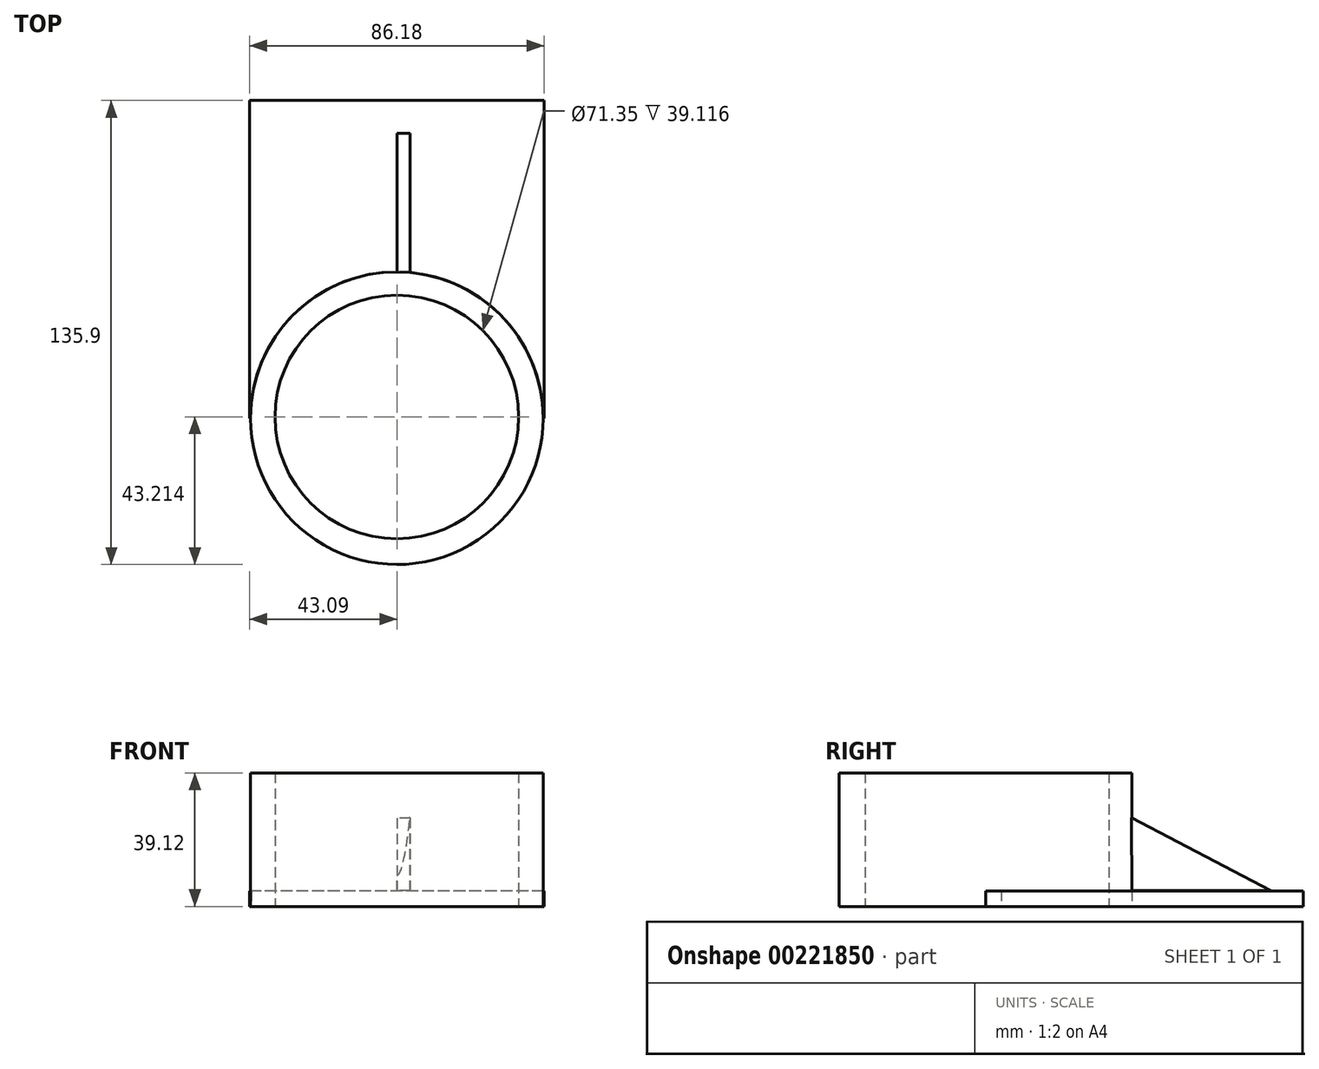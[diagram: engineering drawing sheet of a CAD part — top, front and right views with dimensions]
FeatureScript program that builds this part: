
annotation { "Feature Type Name" : "Feature", "Feature Type Description" : "" }
export const myFeature = defineFeature(function(context is Context, id is Id, definition is map)
    precondition{}
    {
        {
            var Q0;
            Q0=qCreatedBy(makeId("Top.planeOp"),FACE);
            var sketch = newSketch(context, id + "F0", { "sketchPlane" : qUnion([Q0])});
            skLineSegment(sketch, "E0.bottom", {"start": v(43.09, 46.52) * mm, "end": v(-43.09, 46.52) * mm});
            skLineSegment(sketch, "E0.top", {"start": v(43.09, -46.52) * mm, "end": v(42.83, -46.52) * mm});
            skLineSegment(sketch, "E0.left", {"start": v(43.09, 46.52) * mm, "end": v(43.09, -46.52) * mm});
            skLineSegment(sketch, "E0.right", {"start": v(-43.09, 46.52) * mm, "end": v(-43.09, -46.52) * mm});
            skPoint(sketch, "E0.middle", {"position": v(0, 0) * mm});
            skCircle(sketch, "E1", {"center": v(0, -46.52) * mm, "radius": 42.83 * mm});
            skLineSegment(sketch, "E2.trimOffspring", {"start": v(-42.83, -46.52) * mm, "end": v(-43.09, -46.52) * mm});
            skSolve(sketch);
        }
        {
            var Q0;
            Q0=makeQuery(id+"F0.imprint","IMPRINT",FACE,{"disambiguationData":[TD([[makeQuery(id+"F0.imprint","IMPRINT",EDGE,{"derivedFrom":sQuery(id+"F0.wireOp",EDGE,"E0.bottom")}),1.0]])]});
            extrude(context, id + "F1", {"entities" : qUnion([Q0]), "depth" : 4.57 * mm});
        }
        {
            var Q0;
            Q0=qCreatedBy(makeId("Top.planeOp"),FACE);
            var sketch = newSketch(context, id + "F2", { "sketchPlane" : qUnion([Q0])});
            skCircle(sketch, "E3", {"center": v(0, -46.54) * mm, "radius": 42.83 * mm});
            skSolve(sketch);
        }
        {
            var Q0;
            Q0=makeQuery(id+"F2.imprint","IMPRINT",FACE,{"disambiguationData":[TD([[makeQuery(id+"F2.imprint","IMPRINT",EDGE,{"derivedFrom":sQuery(id+"F2.wireOp",EDGE,"E3")}),1.0]])]});
            extrude(context, id + "F3", {"entities" : qUnion([Q0]), "operationType" : NewBodyOperationType.ADD, "depth" : 39.12 * mm});
        }
        {
            var Q0;
            Q0=qCreatedBy(makeId("Top.planeOp"),FACE);
            var sketch = newSketch(context, id + "F4", { "sketchPlane" : qUnion([Q0])});
            skCircle(sketch, "E4", {"center": v(0, -46.17) * mm, "radius": 35.68 * mm});
            skSolve(sketch);
        }
        {
            var Q0;
            Q0 = qSketchRegion(id + "F4", true);
            extrude(context, id + "F5", {"entities" : qUnion([Q0]), "operationType" : NewBodyOperationType.REMOVE, "depth" : 82.55 * mm});
        }
        {
            var Q0;
            Q0=qCreatedBy(makeId("Right.planeOp"),FACE);
            var sketch = newSketch(context, id + "F6", { "sketchPlane" : qUnion([Q0])});
            skLineSegment(sketch, "E5", {"start": v(-3.89, 25.93) * mm, "end": v(36.9, 4.6) * mm});
            skLineSegment(sketch, "E6", {"start": v(36.9, 4.6) * mm, "end": v(-3.66, 4.6) * mm});
            skLineSegment(sketch, "E7", {"start": v(-3.66, 4.6) * mm, "end": v(-3.89, 25.93) * mm});
            skSolve(sketch);
        }
        {
            var Q0;
            Q0=makeQuery(id+"F6.imprint","IMPRINT",FACE,{"disambiguationData":[TD([[makeQuery(id+"F6.imprint","IMPRINT",EDGE,{"derivedFrom":sQuery(id+"F6.wireOp",EDGE,"E5")}),-1.0]])]});
            extrude(context, id + "F7", {"entities" : qUnion([Q0]), "operationType" : NewBodyOperationType.ADD, "depth" : 3.8 * mm});
        }
    });
